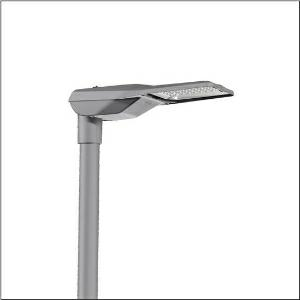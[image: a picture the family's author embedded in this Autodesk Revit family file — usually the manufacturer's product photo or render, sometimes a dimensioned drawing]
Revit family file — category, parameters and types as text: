
# Revit family: streetlight_sl_21_mini___p1_0a_5xe2a33s08gb_ad59
name_source: partatom
category: Lighting Fixtures
units: mm (PartAtom-declared; Revit-internal decimal feet)

## family parameters
Cut with Voids When Loaded = No
Host = Face
Light Source = No
Part Type = Normal
Room Calculation Point = No
Round Connector Dimension = Use Diameter
Shared = No

## types (1)
- --- (1 x LED, 5940 lm, 40.4 W, 3000K)
    Apparent Load = 40 VA
    CIE Flux Codes = 21 50 90 100 100
    Color Rendering = 70
    Color Temperature = 3000K
    Default Elevation = 1800 mm
    Description = Streetlight SL 21 mini, mast luminaire, primary light control with lens, of PMMA, primary optical cover: cover, of toughened safety glass, transparent, light distribution: P1.0a, light emission: direct distribution, primary light characteristic: asymmetric, installation type: side-entry, post-top, LED, High Power LED, rated luminous flux: 5.940lm, luminous efficacy: 147lm/W, light colour: 730, colour temperature: 3000K, control gear: ECG Smart Interface, control: overheat protection, constant luminous flux control, time-dependent luminous flux control, flexible luminous flux parameterisation, mains connection: 220..240V, AC, 50/60Hz, start of lifetime: 40W, end of lifetime: 41W, reduction: 19W, luminaire housing, of diecast aluminium, powder-coated, Siteco® metallic grey (DB 702S), corrosivity category C5 according to DIN EN ISO 12944, length: 628mm, width: 235mm, height: 110mm, spigot size: 60/76mm (post-top) and 42/60/76mm (side-entry), mast flange for spigot size: 42mm: 5XC10008XM4, 60mm: 5XC10008XM2, 76/60mm: 5XC10108XM1, protection rating (complete): IP66, insulation class (complete): insulation class II (safety insulation), certification: CE, ENEC, VDE, impact resistance: IK09, permissible operating ambient temperature for outdoor applications: -40..+50°C, standard-compliant lighting for roads and squares, packaging unit: 1 piece

Light Distribution: P1.0a
    Height = 110 mm
    Lamp = 1 x LED
    Lamp Light Flux = 5940 lm
    Lamp Power = 40.4 W
    Lamp count = 1
    Length = 625 mm
    Luminous efficacy = 147 lm/W
    Manufacturer = Siteco
    ModVariant = No
    Model = 5XE2A33S08GB
    Number of Poles = 1
    OnlyDefault = Yes
    Power Factor = 1
    Product Name = Streetlight SL 21 mini | P1.0a
    Product group = mast luminaire | pylon top
    ProductGroupID = 6100
    Protection Class = Protection class II
    Protection Degree = IP 66
    RLX_Detail_Level = 1
    RlxData = <blob elided: 103273 chars, md5=6088794f>
    Socket = socket
    Standby Power = 0 W
    System Light Flux = 5940 lm
    System Power = 40 W
    Type Comments = factory setting: luminous flux: 100 % | dim-lin: 254 | 812 mA
    Type Image = l_1003515.jpg
    URL = http://relux.com
    VarID = @adj_103773
    Voltage = 0 V
    Weight = 0.00 kg
    Width = 234 mm

## geometry (parser evidence)
native form markers: Blend x4, Sweep x10
no freeform markers — native parametric forms only
